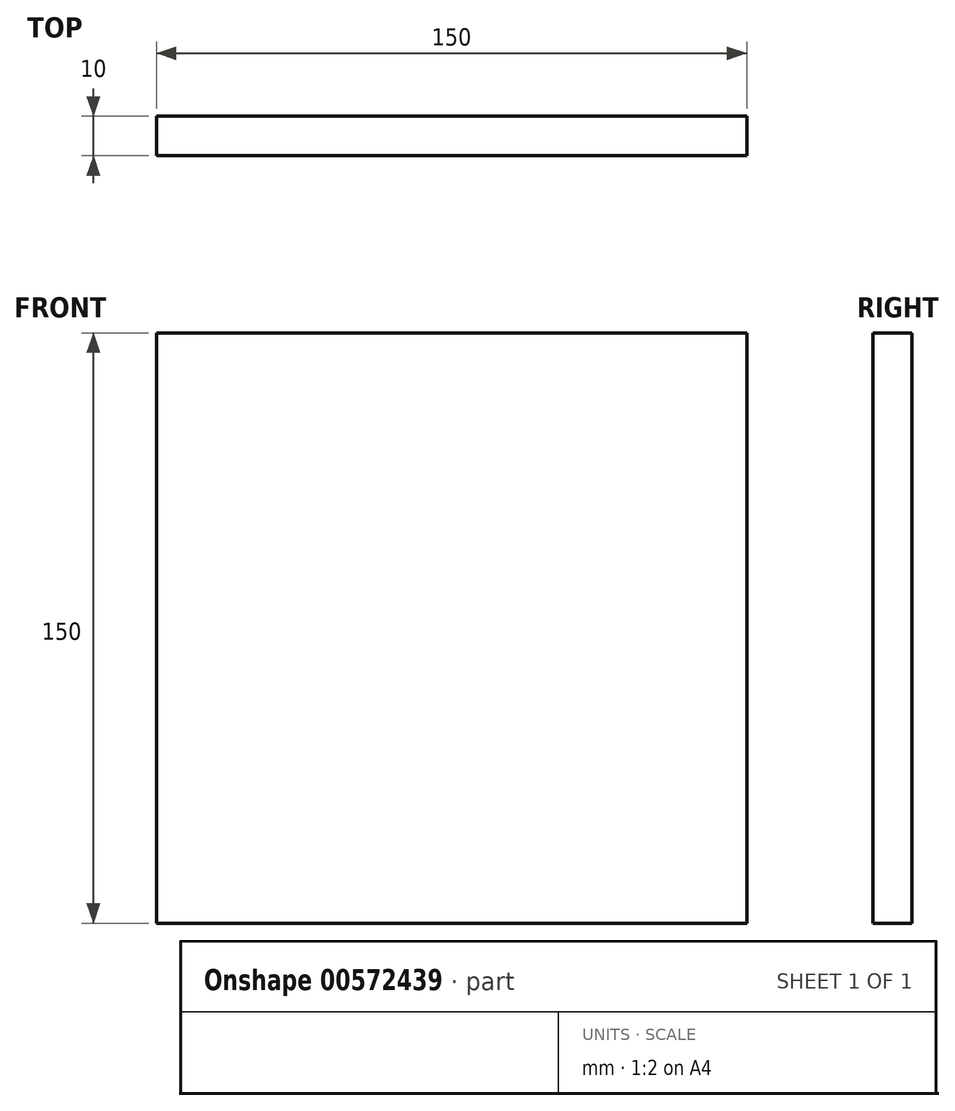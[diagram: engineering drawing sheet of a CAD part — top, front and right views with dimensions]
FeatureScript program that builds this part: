
annotation { "Feature Type Name" : "Feature", "Feature Type Description" : "" }
export const myFeature = defineFeature(function(context is Context, id is Id, definition is map)
    precondition{}
    {
        {
            var Q0;
            Q0=qCreatedBy(makeId("Front.planeOp"),FACE);
            var sketch = newSketch(context, id + "F0", { "sketchPlane" : qUnion([Q0])});
            skLineSegment(sketch, "E0.bottom", {"start": v(-75, 74.55) * mm, "end": v(75, 74.55) * mm});
            skLineSegment(sketch, "E0.top", {"start": v(-75, -75.45) * mm, "end": v(75, -75.45) * mm});
            skLineSegment(sketch, "E0.left", {"start": v(-75, 74.55) * mm, "end": v(-75, -75.45) * mm});
            skLineSegment(sketch, "E0.right", {"start": v(75, 74.55) * mm, "end": v(75, -75.45) * mm});
            skSolve(sketch);
        }
        {
            var Q0;
            Q0 = qSketchRegion(id + "F0", true);
            extrude(context, id + "F1", {"entities" : qUnion([Q0]), "depth" : 10 * mm, "offsetDistance" : 25 * mm});
        }
    });
